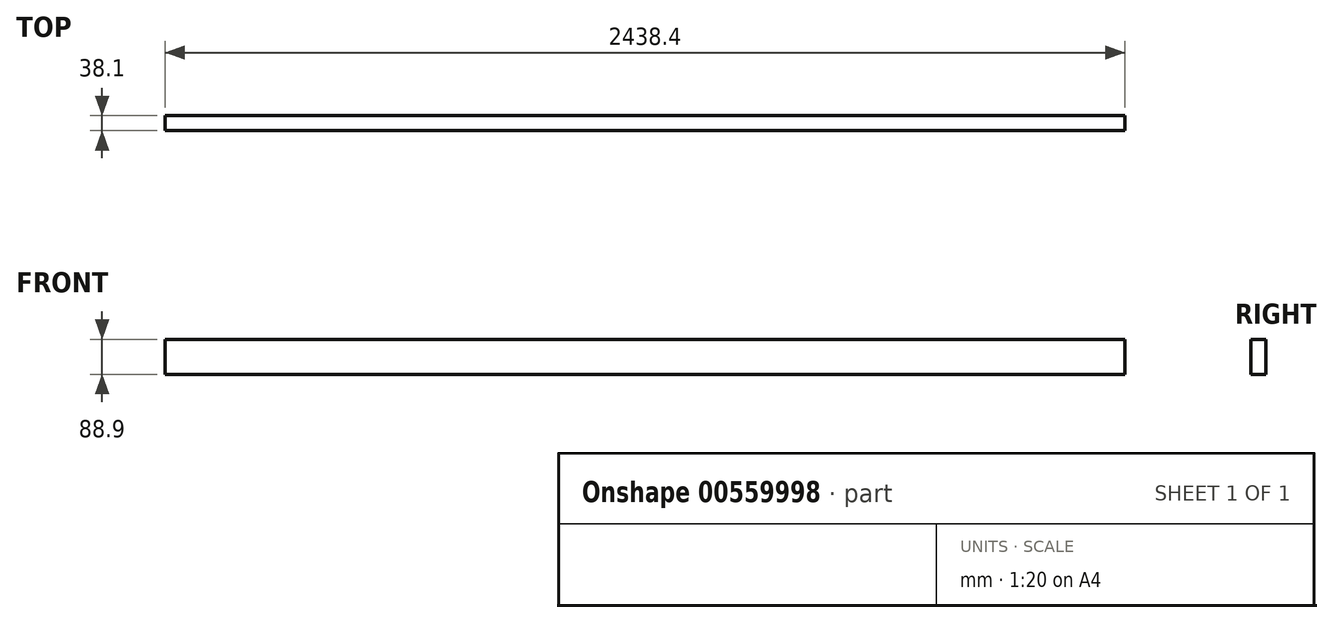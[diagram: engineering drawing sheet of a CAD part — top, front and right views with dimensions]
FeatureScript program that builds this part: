
annotation { "Feature Type Name" : "Feature", "Feature Type Description" : "" }
export const myFeature = defineFeature(function(context is Context, id is Id, definition is map)
    precondition{}
    {
        {
            var Q0;
            Q0=qCreatedBy(makeId("Right.planeOp"),FACE);
            var sketch = newSketch(context, id + "F0", { "sketchPlane" : qUnion([Q0])});
            skLineSegment(sketch, "E0.bottom", {"start": v(19.05, -44.45) * mm, "end": v(-19.05, -44.45) * mm});
            skLineSegment(sketch, "E0.top", {"start": v(19.05, 44.45) * mm, "end": v(-19.05, 44.45) * mm});
            skLineSegment(sketch, "E0.left", {"start": v(19.05, -44.45) * mm, "end": v(19.05, 44.45) * mm});
            skLineSegment(sketch, "E0.right", {"start": v(-19.05, -44.45) * mm, "end": v(-19.05, 44.45) * mm});
            skPoint(sketch, "E0.middle", {"position": v(0, 0) * mm});
            skSolve(sketch);
        }
        {
            var Q0;
            Q0 = qSketchRegion(id + "F0", true);
            extrude(context, id + "F1", {"entities" : qUnion([Q0]), "endBound" : BoundingType.SYMMETRIC, "depth" : 2438.4 * mm, "offsetDistance" : 25.4 * mm});
        }
    });
